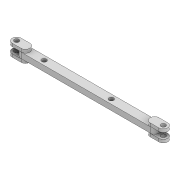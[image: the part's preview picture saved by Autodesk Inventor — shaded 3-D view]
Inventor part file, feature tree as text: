
AUTODESK INVENTOR PART (.ipt)
format: ipt  version: 2022 (Build 260153000, 153)  size: 163,328 bytes
history: native  units: mm
features: extrude x6, sketch x2, projected_geometry x2
ambient origin geometry x8: Origin, YZ Plane, XZ Plane, XY Plane, X Axis, Y Axis, Z Axis, Center Point
bodies: Solid1 (feature_tree)
feature tree (10):
  extrude  "Extrusion1"  Depth=8.0mm
  sketch  "Sketch2"  dims[d0=132.801mm d1=8.0mm]
  extrude  "Extrusion2"  Depth=5.0mm TaperAngle=0.0deg
  sketch  "Sketch3"  dims[d2=4.2mm d4=5.0mm d5=0.0mm d8=4.2mm d9=24.881mm d10=4.2mm d11=8.0mm d12=8.0mm d13=8.0mm d14=3.0mm d15=0.0mm d16=8.0mm d17=8.0mm d18=8.0mm d19=8.0mm d20=3.0mm d21=0.0mm d22=5.0mm d23=0.0mm d24=0.2mm d25=0.0mm d26=0.2mm d27=0.0mm d28=4.2mm d29=85.672mm]
  extrude  "Extrusion3"  Depth=85.672mm
  extrude  "Extrusion4"  Depth=24.881mm
  extrude  "Extrusion5"  Depth=85.672mm
  extrude  "Extrusion6"  Depth=8.0mm
  projected_geometry  "Projected Loop1"
  projected_geometry  "Projected Loop2"
